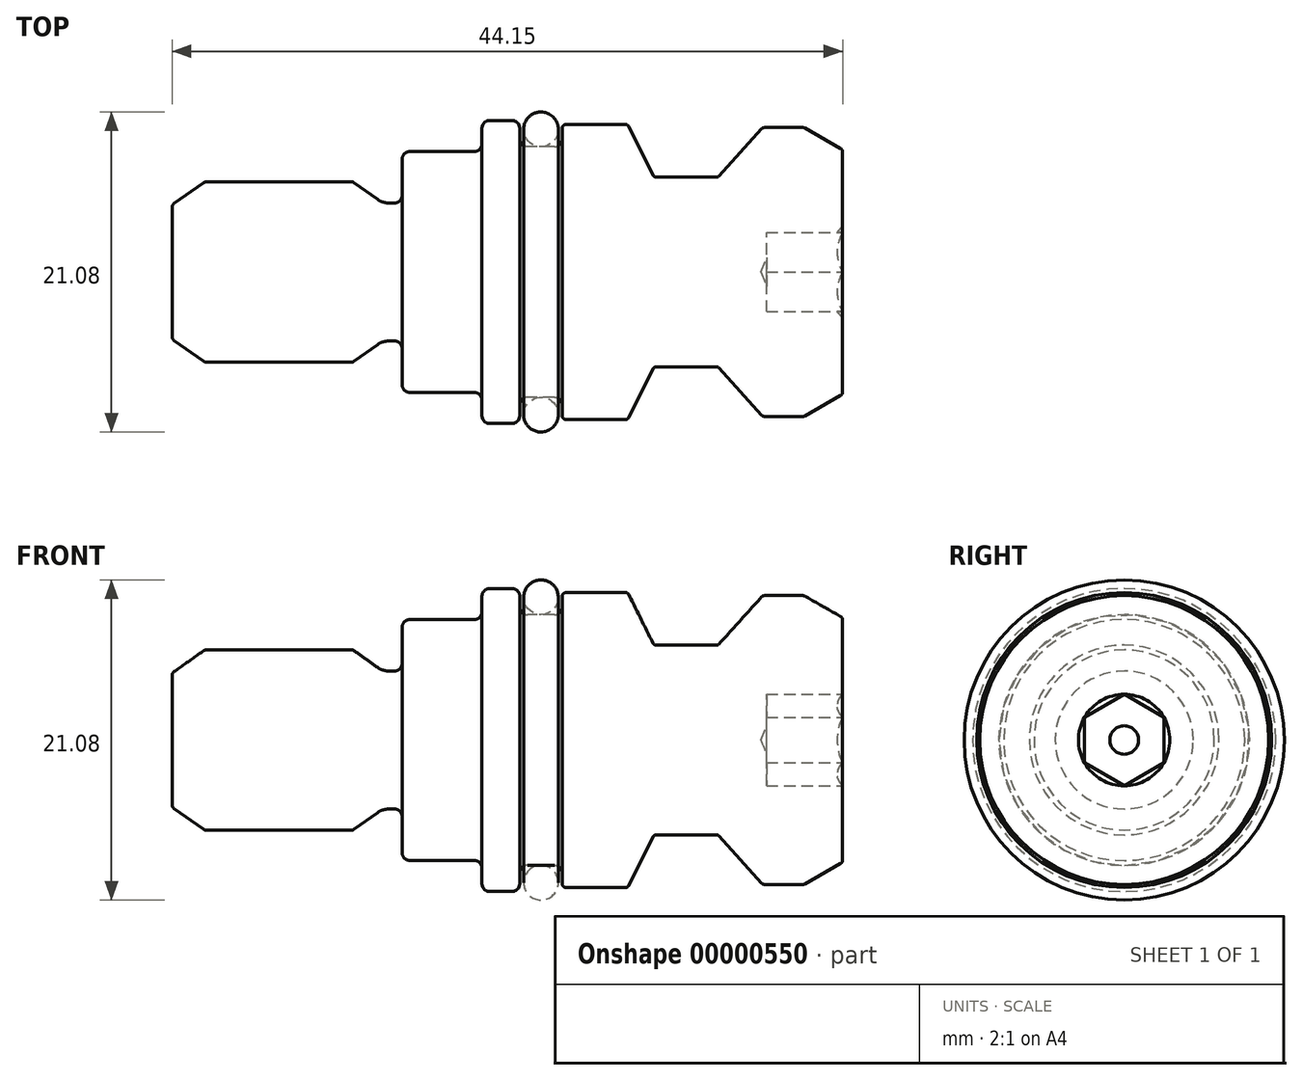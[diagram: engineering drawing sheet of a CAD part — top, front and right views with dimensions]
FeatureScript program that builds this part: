
annotation { "Feature Type Name" : "Feature", "Feature Type Description" : "" }
export const myFeature = defineFeature(function(context is Context, id is Id, definition is map)
    precondition{}
    {
        {
            var Q0;
            Q0 = qCreatedBy(makeId("Front.planeOp"), FACE);
            var sketch = newSketch(context, id + "F0", { "sketchPlane" : qUnion([Q0])});
            skLineSegment(sketch, "E0", {"start": v(0, 0) * mm, "end": v(44.15, 0) * mm});
            skLineSegment(sketch, "E1", {"start": v(44.15, 0) * mm, "end": v(44.15, 7.92) * mm});
            skLineSegment(sketch, "E2", {"start": v(0, 0) * mm, "end": v(0, 4.29) * mm});
            skLineSegment(sketch, "E3", {"start": v(2.13, 0) * mm, "end": v(2.13, 5.93) * mm, "construction": true});
            skLineSegment(sketch, "E4", {"start": v(0.1, 4.5) * mm, "end": v(2.07, 5.88) * mm});
            skLineSegment(sketch, "E5", {"start": v(2.21, 5.93) * mm, "end": v(11.83, 5.93) * mm});
            skLineSegment(sketch, "E6", {"start": v(11.91, 5.93) * mm, "end": v(11.91, 0) * mm, "construction": true});
            skLineSegment(sketch, "E7", {"start": v(13.51, 0) * mm, "end": v(13.51, 4.79) * mm, "construction": true});
            skLineSegment(sketch, "E8", {"start": v(13.51, 4.79) * mm, "end": v(11.98, 5.88) * mm});
            skArc(sketch, "E9", {"start": v(13.51, 4.79) * mm, "mid": v(13.87, 4.6) * mm, "end": v(14.27, 4.54) * mm});
            skLineSegment(sketch, "E10", {"start": v(14.27, 0) * mm, "end": v(14.27, 4.54) * mm, "construction": true});
            skLineSegment(sketch, "E11", {"start": v(14.27, 4.54) * mm, "end": v(14.63, 4.54) * mm});
            skLineSegment(sketch, "E12", {"start": v(15.14, 4.54) * mm, "end": v(15.14, 0) * mm, "construction": true});
            skLineSegment(sketch, "E13", {"start": v(41.54, 9.51) * mm, "end": v(39, 9.51) * mm});
            skLineSegment(sketch, "E14", {"start": v(41.66, 9.48) * mm, "end": v(44.02, 8.14) * mm});
            skLineSegment(sketch, "E15", {"start": v(38.89, 9.51) * mm, "end": v(38.89, 0) * mm, "construction": true});
            skLineSegment(sketch, "E16", {"start": v(30.07, 9.57) * mm, "end": v(31.65, 6.39) * mm});
            skLineSegment(sketch, "E17", {"start": v(36.02, 6.33) * mm, "end": v(38.81, 9.43) * mm});
            skLineSegment(sketch, "E18", {"start": v(31.88, 6.25) * mm, "end": v(35.83, 6.25) * mm});
            skLineSegment(sketch, "E19", {"start": v(29.84, 9.72) * mm, "end": v(25.93, 9.72) * mm});
            skLineSegment(sketch, "E20", {"start": v(25.68, 9.46) * mm, "end": v(25.68, 8.76) * mm});
            skLineSegment(sketch, "E21", {"start": v(25.17, 8.26) * mm, "end": v(23.4, 8.26) * mm});
            skLineSegment(sketch, "E22", {"start": v(22.89, 8.76) * mm, "end": v(22.89, 9.47) * mm});
            skLineSegment(sketch, "E23", {"start": v(22.38, 9.98) * mm, "end": v(20.9, 9.98) * mm});
            skLineSegment(sketch, "E24", {"start": v(20.4, 9.47) * mm, "end": v(20.4, 8.45) * mm});
            skLineSegment(sketch, "E25", {"start": v(19.89, 7.94) * mm, "end": v(15.65, 7.94) * mm});
            skLineSegment(sketch, "E26", {"start": v(15.14, 7.43) * mm, "end": v(15.14, 5.05) * mm});
            skLineSegment(sketch, "E27", {"start": v(22.89, 8.26) * mm, "end": v(22.89, 0) * mm, "construction": true});
            skLineSegment(sketch, "E28", {"start": v(20.4, 7.94) * mm, "end": v(20.4, 0) * mm, "construction": true});
            skPoint(sketch, "E29.orphan", {"position": v(25.68, 0) * mm});
            skPoint(sketch, "E30.visualSharp", {"position": v(15.14, 4.54) * mm});
            skArc(sketch, "E30.filletArc", {"start": v(14.63, 4.54) * mm, "mid": v(14.99, 4.7) * mm, "end": v(15.14, 5.05) * mm});
            skPoint(sketch, "E31.visualSharp", {"position": v(15.14, 7.94) * mm});
            skArc(sketch, "E31.filletArc", {"start": v(15.65, 7.94) * mm, "mid": v(15.29, 7.79) * mm, "end": v(15.14, 7.43) * mm});
            skPoint(sketch, "E32.visualSharp", {"position": v(20.4, 7.94) * mm});
            skArc(sketch, "E32.filletArc", {"start": v(19.89, 7.94) * mm, "mid": v(20.25, 8.09) * mm, "end": v(20.4, 8.45) * mm});
            skPoint(sketch, "E33.visualSharp", {"position": v(20.4, 9.98) * mm});
            skArc(sketch, "E33.filletArc", {"start": v(20.9, 9.98) * mm, "mid": v(20.54, 9.83) * mm, "end": v(20.4, 9.47) * mm});
            skPoint(sketch, "E34.visualSharp", {"position": v(22.89, 9.98) * mm});
            skArc(sketch, "E34.filletArc", {"start": v(22.89, 9.47) * mm, "mid": v(22.74, 9.83) * mm, "end": v(22.38, 9.98) * mm});
            skPoint(sketch, "E35.visualSharp", {"position": v(22.89, 8.26) * mm});
            skArc(sketch, "E35.filletArc", {"start": v(22.89, 8.76) * mm, "mid": v(23.03, 8.4) * mm, "end": v(23.4, 8.25) * mm});
            skPoint(sketch, "E36.visualSharp", {"position": v(25.68, 8.26) * mm});
            skArc(sketch, "E36.filletArc", {"start": v(25.17, 8.26) * mm, "mid": v(25.53, 8.4) * mm, "end": v(25.68, 8.76) * mm});
            skPoint(sketch, "E37.visualSharp", {"position": v(25.68, 9.72) * mm});
            skArc(sketch, "E37.filletArc", {"start": v(25.93, 9.72) * mm, "mid": v(25.75, 9.64) * mm, "end": v(25.68, 9.46) * mm});
            skPoint(sketch, "E38.visualSharp", {"position": v(30, 9.72) * mm});
            skArc(sketch, "E38.filletArc", {"start": v(30.07, 9.57) * mm, "mid": v(29.97, 9.68) * mm, "end": v(29.84, 9.72) * mm});
            skPoint(sketch, "E39.visualSharp", {"position": v(31.72, 6.25) * mm});
            skArc(sketch, "E39.filletArc", {"start": v(31.65, 6.39) * mm, "mid": v(31.75, 6.29) * mm, "end": v(31.88, 6.25) * mm});
            skPoint(sketch, "E40.visualSharp", {"position": v(35.94, 6.25) * mm});
            skArc(sketch, "E40.filletArc", {"start": v(35.83, 6.25) * mm, "mid": v(35.93, 6.27) * mm, "end": v(36.02, 6.33) * mm});
            skPoint(sketch, "E41.visualSharp", {"position": v(38.89, 9.51) * mm});
            skArc(sketch, "E41.filletArc", {"start": v(39, 9.51) * mm, "mid": v(38.9, 9.5) * mm, "end": v(38.81, 9.43) * mm});
            skPoint(sketch, "E42.visualSharp", {"position": v(41.6, 9.51) * mm});
            skArc(sketch, "E42.filletArc", {"start": v(41.66, 9.48) * mm, "mid": v(41.6, 9.5) * mm, "end": v(41.54, 9.51) * mm});
            skPoint(sketch, "E43.visualSharp", {"position": v(44.15, 8.06) * mm});
            skArc(sketch, "E43.filletArc", {"start": v(44.15, 7.92) * mm, "mid": v(44.11, 8.04) * mm, "end": v(44.02, 8.14) * mm});
            skPoint(sketch, "E44.visualSharp", {"position": v(2.13, 5.93) * mm});
            skArc(sketch, "E44.filletArc", {"start": v(2.21, 5.93) * mm, "mid": v(2.14, 5.92) * mm, "end": v(2.07, 5.88) * mm});
            skPoint(sketch, "E45.visualSharp", {"position": v(0, 4.42) * mm});
            skArc(sketch, "E45.filletArc", {"start": v(0.1, 4.5) * mm, "mid": v(0.03, 4.4) * mm, "end": v(0, 4.29) * mm});
            skPoint(sketch, "E46.visualSharp", {"position": v(11.91, 5.93) * mm});
            skArc(sketch, "E46.filletArc", {"start": v(11.98, 5.88) * mm, "mid": v(11.9, 5.92) * mm, "end": v(11.83, 5.93) * mm});
            skLineSegment(sketch, "E47", {"start": v(44.15, 0.94) * mm, "end": v(39.14, 0.94) * mm});
            skLineSegment(sketch, "E48", {"start": v(39.14, 0.94) * mm, "end": v(38.76, 0) * mm});
            skSolve(sketch);
        }
        {
            var Q0;
            {var subQ3=sQuery(id+"F0.wireOp",EDGE,"E2");Q0=makeQuery(id+"F0.imprint","IMPRINT",FACE,{"disambiguationData":[TD([[makeQuery(id+"F0.imprint","IMPRINT",EDGE,{"derivedFrom":subQ3}),-1.0]])]});}
            var Q1;
            Q1=sQuery(id+"F0.wireOp",EDGE,"E0");
            revolve(context, id + "F1", {"entities" : qUnion([Q0]), "axis" : qUnion([Q1]), "revolveType" : RevolveType.FULL});
        }
        {
            var Q0;
            Q0=makeQuery(id+"F1.opRevolve","SWEPT_FACE",FACE,{"disambiguationData":[OSD([sQuery(id+"F0.wireOp",EDGE,"E1")])]});
            var sketch = newSketch(context, id + "F2", { "sketchPlane" : qUnion([Q0])});
            skCircle(sketch, "E49.cCircle", {"center": v(0, 0) * mm, "radius": 3 * mm, "construction": true});
            skLineSegment(sketch, "E49.0", {"start": v(0, 3) * mm, "end": v(2.6, 1.5) * mm});
            skLineSegment(sketch, "E49.1", {"start": v(2.6, 1.5) * mm, "end": v(2.6, -1.5) * mm});
            skLineSegment(sketch, "E49.2", {"start": v(2.6, -1.5) * mm, "end": v(0, -3) * mm});
            skLineSegment(sketch, "E49.3", {"start": v(0, -3) * mm, "end": v(-2.6, -1.5) * mm});
            skLineSegment(sketch, "E49.4", {"start": v(-2.6, -1.5) * mm, "end": v(-2.6, 1.5) * mm});
            skLineSegment(sketch, "E49.5", {"start": v(-2.6, 1.5) * mm, "end": v(0, 3) * mm});
            skSolve(sketch);
        }
        {
            var Q0;
            {var subQ0=makeQuery(id+"F2.imprint","IMPRINT",EDGE,{"derivedFrom":makeQuery(id+"F1.opRevolve","SWEPT_EDGE",EDGE,{"disambiguationData":[OSD([sQuery(id+"F0.wireOp",EDGE,"E1"),sQuery(id+"F0.wireOp",EDGE,"E47")])]})});Q0=qUnion([makeQuery(id+"F2.imprint","IMPRINT",FACE,{"disambiguationData":[TD([[subQ0,-1.0]])]}),makeQuery(id+"F2.imprint","IMPRINT",FACE,{"disambiguationData":[TD([[makeQuery(id+"F2.imprint","IMPRINT",EDGE,{"derivedFrom":sQuery(id+"F2.wireOp",EDGE,"E49.0")}),-1.0]])]})]);}
            extrude(context, id + "F3", {"entities" : qUnion([Q0]), "operationType" : NewBodyOperationType.REMOVE, "oppositeDirection" : true, "depth" : 5 * mm});
        }
        {
            var Q0;
            Q0 = qCreatedBy(makeId("Front.planeOp"), FACE);
            var sketch = newSketch(context, id + "F4", { "sketchPlane" : qUnion([Q0])});
            skPoint(sketch, "E50.0", {"position": v(44.15, 3) * mm});
            skPoint(sketch, "E50.1", {"position": v(44.15, -3) * mm});
            skArc(sketch, "E51", {"start": v(44.15, 3) * mm, "mid": v(42.88, 0) * mm, "end": v(44.15, -3) * mm});
            skLineSegment(sketch, "E52", {"start": v(44.15, -3) * mm, "end": v(44.15, 0) * mm});
            skLineSegment(sketch, "E53", {"start": v(44.15, 0) * mm, "end": v(42.88, 0) * mm});
            skSolve(sketch);
        }
        {
            var Q0;
            {var subQ1=sQuery(id+"F4.wireOp",EDGE,"E52");Q0=makeQuery(id+"F4.imprint","IMPRINT",FACE,{"disambiguationData":[TD([[makeQuery(id+"F4.imprint","IMPRINT",EDGE,{"derivedFrom":subQ1}),1.0]])]});}
            var Q1;
            Q1=sQuery(id+"F4.wireOp",EDGE,"E53");
            revolve(context, id + "F5", {"operationType" : NewBodyOperationType.REMOVE, "entities" : qUnion([Q0]), "axis" : qUnion([Q1]), "revolveType" : RevolveType.FULL, "oppositeDirection" : true});
        }
        {
            var Q0;
            Q0 = qCreatedBy(makeId("Front.planeOp"), FACE);
            var sketch = newSketch(context, id + "F6", { "sketchPlane" : qUnion([Q0])});
            skCircle(sketch, "E54", {"center": v(24.28, 9.4) * mm, "radius": 1.14 * mm});
            skLineSegment(sketch, "E55.0", {"start": v(23.4, -8.25) * mm, "end": v(23.4, 8.25) * mm, "construction": true});
            skLineSegment(sketch, "E55.1", {"start": v(25.17, -8.26) * mm, "end": v(25.17, 8.26) * mm, "construction": true});
            skLineSegment(sketch, "E56", {"start": v(25.17, 0) * mm, "end": v(23.4, 0) * mm, "construction": true});
            skLineSegment(sketch, "E57", {"start": v(24.28, 0) * mm, "end": v(24.28, 8.25) * mm, "construction": true});
            skLineSegment(sketch, "E58", {"start": v(25.17, 8.25) * mm, "end": v(23.4, 8.25) * mm});
            skSolve(sketch);
        }
        {
            var Q0;
            Q0=makeQuery(id+"F6.imprint","IMPRINT",FACE,{"disambiguationData":[TD([[makeQuery(id+"F6.imprint","IMPRINT",EDGE,{"derivedFrom":sQuery(id+"F6.wireOp",EDGE,"E54")}),1.0]])]});
            var Q1;
            Q1=sQuery(id+"F6.wireOp",EDGE,"E56");
            revolve(context, id + "F7", {"entities" : qUnion([Q0]), "axis" : qUnion([Q1]), "revolveType" : RevolveType.FULL});
        }
    });
